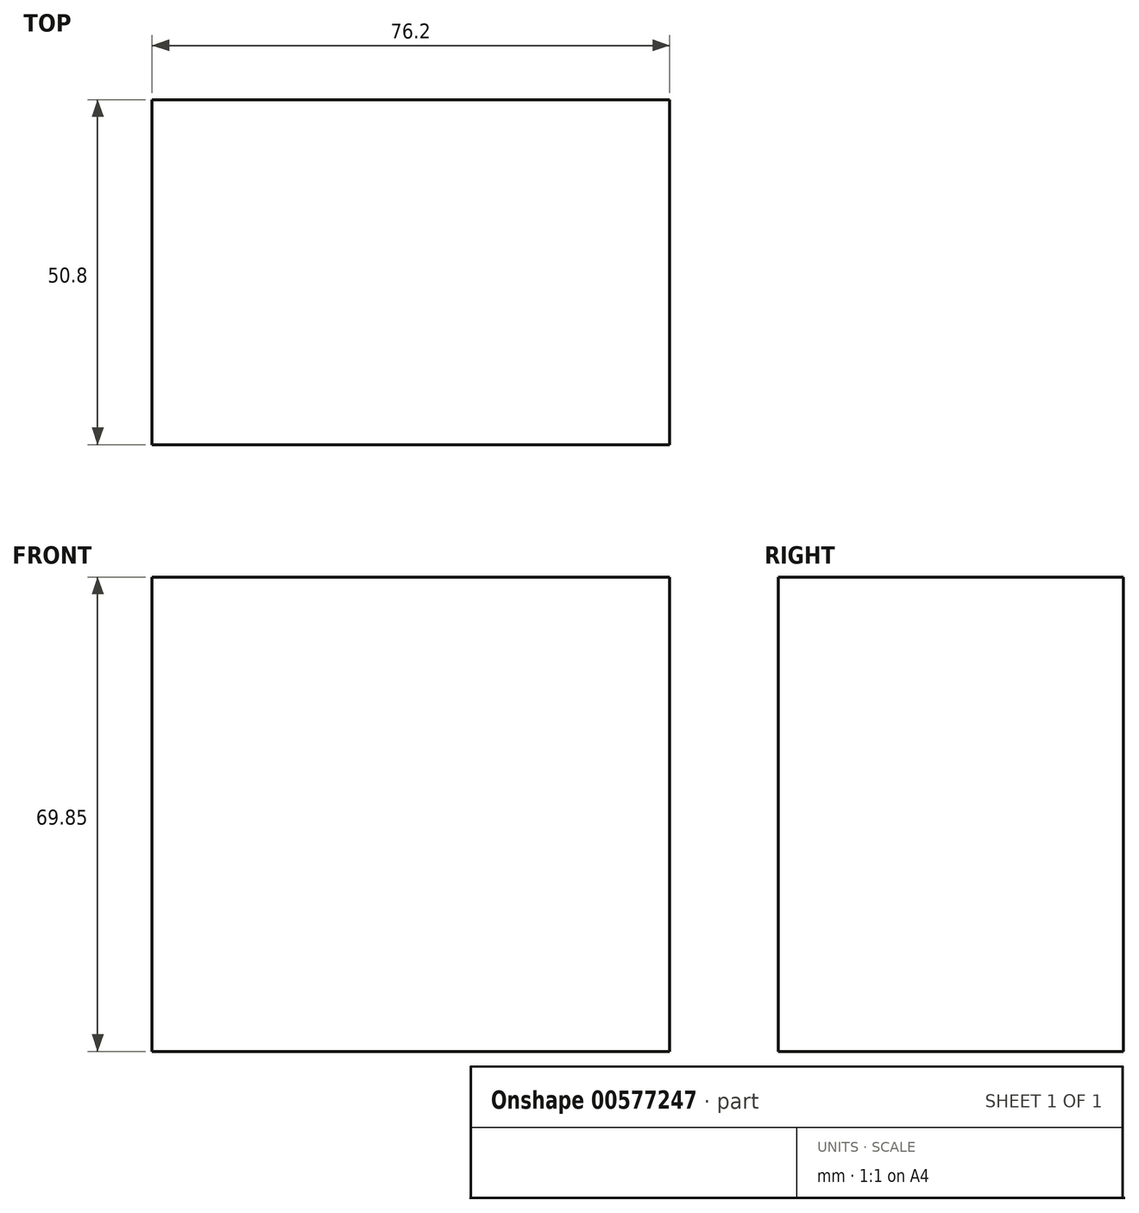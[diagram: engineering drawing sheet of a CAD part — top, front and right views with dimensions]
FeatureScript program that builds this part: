
annotation { "Feature Type Name" : "Feature", "Feature Type Description" : "" }
export const myFeature = defineFeature(function(context is Context, id is Id, definition is map)
    precondition{}
    {
        {
            var Q0;
            Q0=qCreatedBy(makeId("Front.planeOp"),FACE);
            var sketch = newSketch(context, id + "F0", { "sketchPlane" : qUnion([Q0])});
            skLineSegment(sketch, "E0.bottom", {"start": v(-42.01, 29.6) * mm, "end": v(34.19, 29.6) * mm});
            skLineSegment(sketch, "E0.top", {"start": v(-42.01, -40.24) * mm, "end": v(34.19, -40.24) * mm});
            skLineSegment(sketch, "E0.left", {"start": v(-42.01, 29.6) * mm, "end": v(-42.01, -40.24) * mm});
            skLineSegment(sketch, "E0.right", {"start": v(34.19, 29.6) * mm, "end": v(34.19, -40.24) * mm});
            skSolve(sketch);
        }
        {
            var Q0;
            Q0 = qSketchRegion(id + "F0", true);
            extrude(context, id + "F1", {"entities" : qUnion([Q0]), "depth" : 50.8 * mm, "offsetDistance" : 25.4 * mm});
        }
    });
